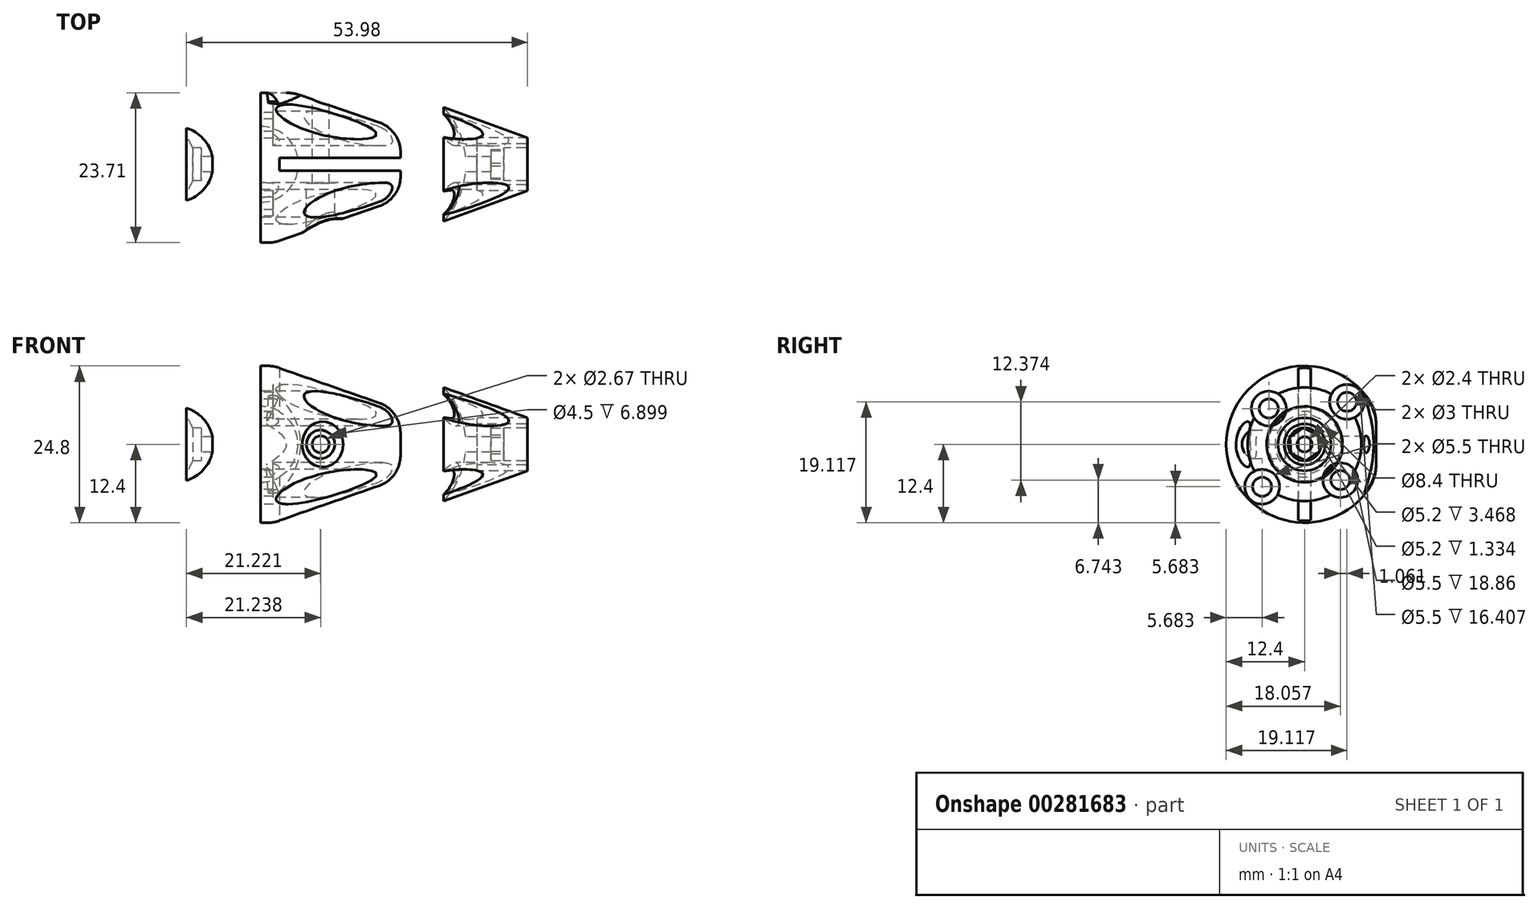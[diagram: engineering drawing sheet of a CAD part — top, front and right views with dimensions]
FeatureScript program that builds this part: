
annotation { "Feature Type Name" : "Feature", "Feature Type Description" : "" }
export const myFeature = defineFeature(function(context is Context, id is Id, definition is map)
    precondition{}
    {
        {
            var Q0;
            Q0=qCreatedBy(makeId("Front.planeOp"),FACE);
            var sketch = newSketch(context, id + "F0", { "sketchPlane" : qUnion([Q0])});
            skLineSegment(sketch, "E0", {"start": v(0, 0) * mm, "end": v(13.34, 0) * mm, "construction": true});
            skPoint(sketch, "E1.orphan", {"position": v(-28.38, 0) * mm});
            skLineSegment(sketch, "E2", {"start": v(0, 6) * mm, "end": v(0, 12.4) * mm});
            skArc(sketch, "E3", {"start": v(6, 0) * mm, "mid": v(4.24, 4.24) * mm, "end": v(0, 6) * mm});
            skLineSegment(sketch, "E4", {"start": v(0, 12.4) * mm, "end": v(1.24, 12.4) * mm});
            skLineSegment(sketch, "E5", {"start": v(0, 0) * mm, "end": v(14.19, 5.16) * mm, "construction": true});
            skLineSegment(sketch, "E6.filletArc", {"start": v(12.16, 5.5) * mm, "end": v(12.16, 5.5) * mm});
            skLineSegment(sketch, "E7", {"start": v(2.88, 12.12) * mm, "end": v(18.8, 6.6) * mm});
            skLineSegment(sketch, "E8", {"start": v(22.16, 1.88) * mm, "end": v(22.16, 0) * mm});
            skLineSegment(sketch, "E9", {"start": v(22.16, 0) * mm, "end": v(6, 0) * mm});
            skPoint(sketch, "E10.visualSharp", {"position": v(2.08, 12.4) * mm});
            skArc(sketch, "E10.filletArc", {"start": v(2.88, 12.12) * mm, "mid": v(2.07, 12.33) * mm, "end": v(1.24, 12.4) * mm});
            skArc(sketch, "E11.filletArc", {"start": v(22.16, 1.88) * mm, "mid": v(21.23, 4.78) * mm, "end": v(18.8, 6.6) * mm});
            skSolve(sketch);
        }
        {
            var Q0;
            Q0 = qSketchRegion(id + "F0", true);
            var Q1;
            Q1=sQuery(id+"F0.wireOp",EDGE,"E0");
            revolve(context, id + "F1", {"entities" : qUnion([Q0]), "axis" : qUnion([Q1]), "revolveType" : RevolveType.FULL});
        }
        {
            var Q0;
            Q0=qCreatedBy(makeId("Right.planeOp"),FACE);
            var sketch = newSketch(context, id + "F2", { "sketchPlane" : qUnion([Q0])});
            skCircle(sketch, "E12", {"center": v(6.72, 6.72) * mm, "radius": 1.5 * mm});
            skCircle(sketch, "E13", {"center": v(5.66, -5.66) * mm, "radius": 1.5 * mm});
            skCircle(sketch, "E14.MirrorC", {"center": v(-5.66, 5.66) * mm, "radius": 1.5 * mm});
            skCircle(sketch, "E15.MirrorC", {"center": v(-6.72, -6.72) * mm, "radius": 1.5 * mm});
            skCircle(sketch, "E16", {"center": v(6.72, 6.72) * mm, "radius": 2.75 * mm});
            skCircle(sketch, "E17", {"center": v(-5.66, 5.66) * mm, "radius": 2.75 * mm});
            skCircle(sketch, "E18", {"center": v(-6.72, -6.72) * mm, "radius": 2.75 * mm});
            skCircle(sketch, "E19", {"center": v(5.66, -5.66) * mm, "radius": 2.75 * mm});
            skSolve(sketch);
        }
        {
            var Q0;
            Q0=qCreatedBy(makeId("Front.planeOp"),FACE);
            var sketch = newSketch(context, id + "F3", { "sketchPlane" : qUnion([Q0])});
            skLineSegment(sketch, "E20", {"start": v(28.99, 9) * mm, "end": v(42.26, 4.2) * mm});
            skLineSegment(sketch, "E21", {"start": v(42.26, 4.2) * mm, "end": v(34.46, 4.2) * mm});
            skLineSegment(sketch, "E22", {"start": v(34.26, 4) * mm, "end": v(34.26, 3.45) * mm});
            skLineSegment(sketch, "E23", {"start": v(34.46, 3.25) * mm, "end": v(42.26, 3.25) * mm});
            skArc(sketch, "E24.trimOffspring", {"start": v(32.45, 1.3) * mm, "mid": v(31.35, 5.43) * mm, "end": v(28.99, 9) * mm});
            skLineSegment(sketch, "E25", {"start": v(38.5, 0) * mm, "end": v(42.26, 0) * mm, "construction": true});
            skLineSegment(sketch, "E26", {"start": v(42.26, 3.25) * mm, "end": v(42.26, 2.6) * mm});
            skPoint(sketch, "E27.visualSharp", {"position": v(42.26, 3.25) * mm});
            skLineSegment(sketch, "E28", {"start": v(32.55, 1.2) * mm, "end": v(38.5, 1.2) * mm});
            skLineSegment(sketch, "E29", {"start": v(38.5, 2.6) * mm, "end": v(38.5, 1.2) * mm});
            skPoint(sketch, "E30.newPointA", {"position": v(32.5, 0.68) * mm});
            skArc(sketch, "E30.filletArc", {"start": v(32.45, 1.3) * mm, "mid": v(32.48, 1.23) * mm, "end": v(32.55, 1.2) * mm});
            skPoint(sketch, "E31.visualSharp", {"position": v(38.5, 1.2) * mm});
            skPoint(sketch, "E32.visualSharp", {"position": v(34.26, 3.25) * mm});
            skArc(sketch, "E32.filletArc", {"start": v(34.26, 3.45) * mm, "mid": v(34.32, 3.3) * mm, "end": v(34.46, 3.25) * mm});
            skPoint(sketch, "E33.visualSharp", {"position": v(34.26, 4.2) * mm});
            skArc(sketch, "E33.filletArc", {"start": v(34.46, 4.2) * mm, "mid": v(34.32, 4.14) * mm, "end": v(34.26, 4) * mm});
            skLineSegment(sketch, "E34", {"start": v(38.5, 2.6) * mm, "end": v(42.26, 2.6) * mm});
            skPoint(sketch, "E35.visualSharp", {"position": v(42.26, 2.6) * mm});
            skSolve(sketch);
        }
        {
            var Q0;
            Q0=makeQuery(id+"F3.imprint","IMPRINT",FACE,{"disambiguationData":[TD([[makeQuery(id+"F3.imprint","IMPRINT",EDGE,{"derivedFrom":sQuery(id+"F3.wireOp",EDGE,"E20")}),-1.0]])]});
            var Q1;
            Q1=sQuery(id+"F3.wireOp",EDGE,"E25");
            revolve(context, id + "F4", {"entities" : qUnion([Q0]), "axis" : qUnion([Q1]), "revolveType" : RevolveType.FULL});
        }
        {
            var Q0;
            Q0=makeQuery(id+"F2.imprint","IMPRINT",FACE,{"disambiguationData":[TD([[makeQuery(id+"F2.imprint","IMPRINT",EDGE,{"derivedFrom":sQuery(id+"F2.wireOp",EDGE,"E12")}),1.0]])]});
            var Q1;
            {var subQ0=sQuery(id+"F2.wireOp",EDGE,"E14.MirrorC");var subQ1=makeQuery(id+"F1.opRevolve","SWEPT_EDGE",EDGE,{"disambiguationData":[OSD([sQuery(id+"F0.wireOp",EDGE,"E2"),sQuery(id+"F0.wireOp",EDGE,"E3")])]});var subQ2=makeQuery(id+"F2.imprint","INTERSECT",VERTEX,{"disambiguationData":[OD(0.0)],"derivedFrom":[subQ1,subQ0]});Q1=makeQuery(id+"F2.imprint","IMPRINT",FACE,{"disambiguationData":[TD([[makeQuery(id+"F2.imprint","IMPRINT",EDGE,{"disambiguationData":[TD([[subQ2,1.0]])],"derivedFrom":subQ0}),-1.0]])]});}
            var Q2;
            {var subQ0=sQuery(id+"F2.wireOp",EDGE,"E14.MirrorC");var subQ1=makeQuery(id+"F1.opRevolve","SWEPT_EDGE",EDGE,{"disambiguationData":[OSD([sQuery(id+"F0.wireOp",EDGE,"E2"),sQuery(id+"F0.wireOp",EDGE,"E3")])]});var subQ2=makeQuery(id+"F2.imprint","INTERSECT",VERTEX,{"disambiguationData":[OD(0.0)],"derivedFrom":[subQ1,subQ0]});Q2=makeQuery(id+"F2.imprint","IMPRINT",FACE,{"disambiguationData":[TD([[makeQuery(id+"F2.imprint","IMPRINT",EDGE,{"disambiguationData":[TD([[subQ2,-1.0]])],"derivedFrom":subQ0}),-1.0]])]});}
            var Q3;
            Q3=makeQuery(id+"F2.imprint","IMPRINT",FACE,{"disambiguationData":[TD([[makeQuery(id+"F2.imprint","IMPRINT",EDGE,{"derivedFrom":sQuery(id+"F2.wireOp",EDGE,"E15.MirrorC")}),-1.0]])]});
            var Q4;
            {var subQ0=sQuery(id+"F2.wireOp",EDGE,"E13");var subQ1=makeQuery(id+"F1.opRevolve","SWEPT_EDGE",EDGE,{"disambiguationData":[OSD([sQuery(id+"F0.wireOp",EDGE,"E2"),sQuery(id+"F0.wireOp",EDGE,"E3")])]});var subQ2=makeQuery(id+"F2.imprint","INTERSECT",VERTEX,{"disambiguationData":[OD(0.0)],"derivedFrom":[subQ1,subQ0]});Q4=makeQuery(id+"F2.imprint","IMPRINT",FACE,{"disambiguationData":[TD([[makeQuery(id+"F2.imprint","IMPRINT",EDGE,{"disambiguationData":[TD([[subQ2,-1.0]])],"derivedFrom":subQ0}),1.0]])]});}
            var Q5;
            {var subQ0=sQuery(id+"F2.wireOp",EDGE,"E13");var subQ1=makeQuery(id+"F1.opRevolve","SWEPT_EDGE",EDGE,{"disambiguationData":[OSD([sQuery(id+"F0.wireOp",EDGE,"E2"),sQuery(id+"F0.wireOp",EDGE,"E3")])]});var subQ2=makeQuery(id+"F2.imprint","INTERSECT",VERTEX,{"disambiguationData":[OD(0.0)],"derivedFrom":[subQ1,subQ0]});Q5=makeQuery(id+"F2.imprint","IMPRINT",FACE,{"disambiguationData":[TD([[makeQuery(id+"F2.imprint","IMPRINT",EDGE,{"disambiguationData":[TD([[subQ2,1.0]])],"derivedFrom":subQ0}),1.0]])]});}
            var Q6;
            Q6=makeQuery(id+"F2.imprint","IMPRINT",FACE,{"disambiguationData":[TD([[makeQuery(id+"F2.imprint","IMPRINT",EDGE,{"derivedFrom":sQuery(id+"F2.wireOp",EDGE,"E14.MirrorC")}),-1.0]])]});
            var Q7;
            Q7=makeQuery(id+"F2.imprint","IMPRINT",FACE,{"disambiguationData":[TD([[makeQuery(id+"F2.imprint","IMPRINT",EDGE,{"derivedFrom":sQuery(id+"F2.wireOp",EDGE,"E13")}),1.0]])]});
            extrude(context, id + "F5", {"entities" : qUnion([Q0, Q1, Q2, Q3, Q4, Q5, Q6, Q7]), "operationType" : NewBodyOperationType.REMOVE, "depth" : 50 * mm, "offsetDistance" : 25 * mm});
        }
        {
            var Q0;
            Q0=makeQuery(id+"F2.imprint","IMPRINT",FACE,{"disambiguationData":[TD([[makeQuery(id+"F2.imprint","IMPRINT",EDGE,{"derivedFrom":sQuery(id+"F2.wireOp",EDGE,"E14.MirrorC")}),1.0]])]});
            var Q1;
            Q1=makeQuery(id+"F2.imprint","IMPRINT",FACE,{"disambiguationData":[TD([[makeQuery(id+"F2.imprint","IMPRINT",EDGE,{"derivedFrom":sQuery(id+"F2.wireOp",EDGE,"E12")}),-1.0]])]});
            var Q2;
            Q2=makeQuery(id+"F2.imprint","IMPRINT",FACE,{"disambiguationData":[TD([[makeQuery(id+"F2.imprint","IMPRINT",EDGE,{"derivedFrom":sQuery(id+"F2.wireOp",EDGE,"E13")}),-1.0]])]});
            var Q3;
            Q3=makeQuery(id+"F2.imprint","IMPRINT",FACE,{"disambiguationData":[TD([[makeQuery(id+"F2.imprint","IMPRINT",EDGE,{"derivedFrom":sQuery(id+"F2.wireOp",EDGE,"E15.MirrorC")}),1.0]])]});
            extrude(context, id + "F6", {"entities" : qUnion([Q0, Q1, Q2, Q3]), "operationType" : NewBodyOperationType.REMOVE, "depth" : 50 * mm, "offsetDistance" : 25 * mm, "hasSecondDirection" : true, "secondDirectionOppositeDirection" : false, "secondDirectionDepth" : 2 * mm});
        }
        {
            var Q0;
            Q0=qCreatedBy(makeId("Front.planeOp"),FACE);
            var sketch = newSketch(context, id + "F7", { "sketchPlane" : qUnion([Q0])});
            skLineSegment(sketch, "E36", {"start": v(-7.6, 1.2) * mm, "end": v(-9.4, 1.2) * mm});
            skPoint(sketch, "E37.orphan", {"position": v(-13.49, 0) * mm});
            skArc(sketch, "E38.trimOffspring", {"start": v(-7.6, 1.2) * mm, "mid": v(-9.04, 4.03) * mm, "end": v(-11.72, 5.73) * mm});
            skLineSegment(sketch, "E39", {"start": v(-10.74, 2.6) * mm, "end": v(-9.4, 2.6) * mm});
            skLineSegment(sketch, "E40", {"start": v(-9.4, 2.6) * mm, "end": v(-9.4, 1.2) * mm});
            skLineSegment(sketch, "E41", {"start": v(-13.49, 0) * mm, "end": v(-6.77, 0) * mm, "construction": true});
            skLineSegment(sketch, "E42", {"start": v(-11.72, 5.73) * mm, "end": v(-11.72, 4.67) * mm});
            skLineSegment(sketch, "E43", {"start": v(-11.72, 4.67) * mm, "end": v(-10.74, 2.6) * mm});
            skSolve(sketch);
        }
        {
            var Q0;
            Q0=makeQuery(id+"F7.imprint","IMPRINT",FACE,{"disambiguationData":[TD([[makeQuery(id+"F7.imprint","IMPRINT",EDGE,{"derivedFrom":sQuery(id+"F7.wireOp",EDGE,"E36")}),-1.0]])]});
            var Q1;
            Q1=sQuery(id+"F7.wireOp",EDGE,"E41");
            revolve(context, id + "F8", {"entities" : qUnion([Q0]), "axis" : qUnion([Q1]), "revolveType" : RevolveType.FULL});
        }
        {
            var Q0;
            Q0=makeQuery(id+"F4.opRevolve","SWEPT_FACE",FACE,{"disambiguationData":[OSD([sQuery(id+"F3.wireOp",EDGE,"E29")])]});
            var sketch = newSketch(context, id + "F9", { "sketchPlane" : qUnion([Q0])});
            skLineSegment(sketch, "E44.2.0", {"start": v(0, 0) * mm, "end": v(-2.35, 1.1) * mm});
            skPoint(sketch, "E44.center", {"position": v(0, 0) * mm});
            skLineSegment(sketch, "E45", {"start": v(-2.35, 1.1) * mm, "end": v(-0.22, 2.6) * mm});
            skLineSegment(sketch, "E46", {"start": v(-0.22, 2.6) * mm, "end": v(2.13, 1.49) * mm});
            skLineSegment(sketch, "E47", {"start": v(2.35, -1.1) * mm, "end": v(2.13, 1.49) * mm});
            skLineSegment(sketch, "E48", {"start": v(2.35, -1.1) * mm, "end": v(0.22, -2.6) * mm});
            skLineSegment(sketch, "E49", {"start": v(0.22, -2.6) * mm, "end": v(-2.13, -1.49) * mm});
            skLineSegment(sketch, "E50", {"start": v(-2.35, 1.1) * mm, "end": v(-2.13, -1.49) * mm});
            skSolve(sketch);
        }
        {
            var Q0;
            Q0=makeQuery(id+"F9.imprint","IMPRINT",FACE,{"disambiguationData":[TD([[makeQuery(id+"F9.imprint","IMPRINT",EDGE,{"derivedFrom":sQuery(id+"F9.wireOp",EDGE,"E45")}),-1.0]])]});
            extrude(context, id + "F10", {"entities" : qUnion([Q0]), "operationType" : NewBodyOperationType.REMOVE, "oppositeDirection" : true, "depth" : 2 * mm, "offsetDistance" : 25 * mm});
        }
        {
            var Q0;
            Q0=makeQuery(id+"F4.opRevolve","SWEPT_FACE",FACE,{"disambiguationData":[OSD([sQuery(id+"F3.wireOp",EDGE,"E26")])]});
            fillet(context, id + "F11", {"entities" : qUnion([Q0]), "radius" : 0.3 * mm, "tangentPropagation" : true, "allowEdgeOverflow" : false});
        }
        {
            var Q0;
            Q0=qCreatedBy(makeId("Right.planeOp"),FACE);
            var sketch = newSketch(context, id + "F12", { "sketchPlane" : qUnion([Q0])});
            skLineSegment(sketch, "E51.bottom", {"start": v(11.3, 6.39) * mm, "end": v(13.77, 6.39) * mm});
            skLineSegment(sketch, "E51.top", {"start": v(11.3, -6.25) * mm, "end": v(13.77, -6.25) * mm});
            skLineSegment(sketch, "E51.left", {"start": v(11.3, 6.39) * mm, "end": v(11.3, -6.25) * mm});
            skLineSegment(sketch, "E51.right", {"start": v(13.77, 6.39) * mm, "end": v(13.77, -6.25) * mm});
            skLineSegment(sketch, "E52.bottom", {"start": v(0, 16.58) * mm, "end": v(-1, 16.58) * mm});
            skLineSegment(sketch, "E52.top", {"start": v(0, -15.36) * mm, "end": v(-1, -15.36) * mm});
            skLineSegment(sketch, "E52.left", {"start": v(0, 16.58) * mm, "end": v(0, -15.36) * mm});
            skLineSegment(sketch, "E52.right", {"start": v(-1, 16.58) * mm, "end": v(-1, -15.36) * mm});
            skLineSegment(sketch, "E53.MirrorCS", {"start": v(1, 16.58) * mm, "end": v(1, -15.36) * mm});
            skLineSegment(sketch, "E54.MirrorCS", {"start": v(0, -15.36) * mm, "end": v(1, -15.36) * mm});
            skLineSegment(sketch, "E55.MirrorCS", {"start": v(0, 16.58) * mm, "end": v(1, 16.58) * mm});
            skSolve(sketch);
        }
        {
            var Q0;
            Q0=makeQuery(id+"F12.imprint","IMPRINT",FACE,{"disambiguationData":[TD([[makeQuery(id+"F12.imprint","IMPRINT",EDGE,{"derivedFrom":sQuery(id+"F12.wireOp",EDGE,"E52.left")}),1.0]])]});
            var Q1;
            Q1=makeQuery(id+"F12.imprint","IMPRINT",FACE,{"disambiguationData":[TD([[makeQuery(id+"F12.imprint","IMPRINT",EDGE,{"derivedFrom":sQuery(id+"F12.wireOp",EDGE,"E52.bottom")}),1.0]])]});
            extrude(context, id + "F13", {"entities" : qUnion([Q0, Q1]), "operationType" : NewBodyOperationType.REMOVE, "depth" : 25 * mm, "offsetDistance" : 25 * mm, "hasSecondDirection" : true, "secondDirectionOppositeDirection" : false, "secondDirectionDepth" : 3 * mm});
        }
        {
            var Q0;
            Q0=makeQuery(id+"F12.imprint","IMPRINT",FACE,{"disambiguationData":[TD([[makeQuery(id+"F12.imprint","IMPRINT",EDGE,{"derivedFrom":sQuery(id+"F12.wireOp",EDGE,"E51.bottom")}),-1.0]])]});
            extrude(context, id + "F14", {"entities" : qUnion([Q0]), "operationType" : NewBodyOperationType.REMOVE, "depth" : 25 * mm, "offsetDistance" : 25 * mm});
        }
        {
            var Q0;
            Q0=qCreatedBy(makeId("Front.planeOp"),FACE);
            var sketch = newSketch(context, id + "F15", { "sketchPlane" : qUnion([Q0])});
            skCircle(sketch, "E56", {"center": v(9.52, 0) * mm, "radius": 1.34 * mm});
            skSolve(sketch);
        }
        {
            var Q0;
            Q0 = qSketchRegion(id + "F15", true);
            extrude(context, id + "F16", {"entities" : qUnion([Q0]), "operationType" : NewBodyOperationType.REMOVE, "depth" : 25 * mm, "offsetDistance" : 25 * mm, "symmetric" : true});
        }
        {
            var Q0;
            Q0=qCreatedBy(makeId("Front.planeOp"),FACE);
            var sketch = newSketch(context, id + "F17", { "sketchPlane" : qUnion([Q0])});
            skCircle(sketch, "E57", {"center": v(9.5, 0) * mm, "radius": 2.25 * mm});
            skSolve(sketch);
        }
        {
            var Q0;
            Q0=makeQuery(id+"F17.imprint","IMPRINT",FACE,{"disambiguationData":[TD([[makeQuery(id+"F17.imprint","IMPRINT",EDGE,{"derivedFrom":sQuery(id+"F17.wireOp",EDGE,"E57")}),1.0]])]});
            extrude(context, id + "F18", {"entities" : qUnion([Q0]), "operationType" : NewBodyOperationType.REMOVE, "depth" : 25 * mm, "offsetDistance" : 25 * mm, "hasSecondDirection" : true, "secondDirectionOppositeDirection" : false, "secondDirectionDepth" : 3 * mm});
        }
        {
            var Q0;
            Q0=makeQuery(id+"F18.boolean.opBoolean","INTERSECT",EDGE,{"derivedFrom":[makeQuery(id+"F1.opRevolve","SWEPT_FACE",FACE,{"disambiguationData":[OSD([sQuery(id+"F0.wireOp",EDGE,"E7")])]}),makeQuery(id+"F18.opExtrude","SWEPT_FACE",FACE,{"disambiguationData":[OSD([sQuery(id+"F17.wireOp",EDGE,"E57")])]})]});
            fillet(context, id + "F19", {"entities" : qUnion([Q0]), "radius" : 1 * mm, "tangentPropagation" : true, "allowEdgeOverflow" : false});
        }
        {
            var Q0;
            Q0=makeQuery(id+"F14.boolean.opBoolean","INTERSECT",EDGE,{"derivedFrom":[makeQuery(id+"F1.opRevolve","SWEPT_FACE",FACE,{"disambiguationData":[OSD([sQuery(id+"F0.wireOp",EDGE,"E7")])]}),makeQuery(id+"F14.opExtrude","SWEPT_FACE",FACE,{"disambiguationData":[OSD([sQuery(id+"F12.wireOp",EDGE,"E51.left")])]})]});
            fillet(context, id + "F20", {"entities" : qUnion([Q0]), "radius" : 7 * mm, "tangentPropagation" : true, "allowEdgeOverflow" : false});
        }
    });
